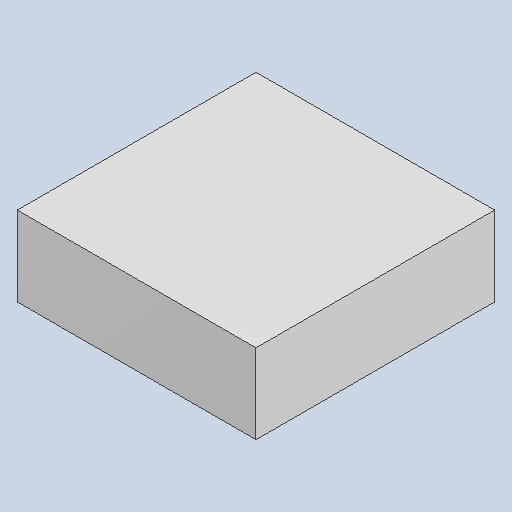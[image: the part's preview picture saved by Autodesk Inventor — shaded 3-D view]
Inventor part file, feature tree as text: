
AUTODESK INVENTOR PART (.ipt)
format: ipt  version: 2023.4 (Build 274418000, 418)  size: 79,872 bytes
history: native  units: mm
features: extrude x1
ambient origin geometry x8: Origin, YZ Plane, XZ Plane, XY Plane, X Axis, Y Axis, Z Axis, Center Point
bodies: Solid1 (feature_tree)
feature tree (1):
  extrude  "Extruded_24"  [1 undecoded]
note: 1 required parameter value undecoded (feature->parameter linkage not recoverable at this tier; creation-order binding heuristic only, values carry confidence <= 0.55)
